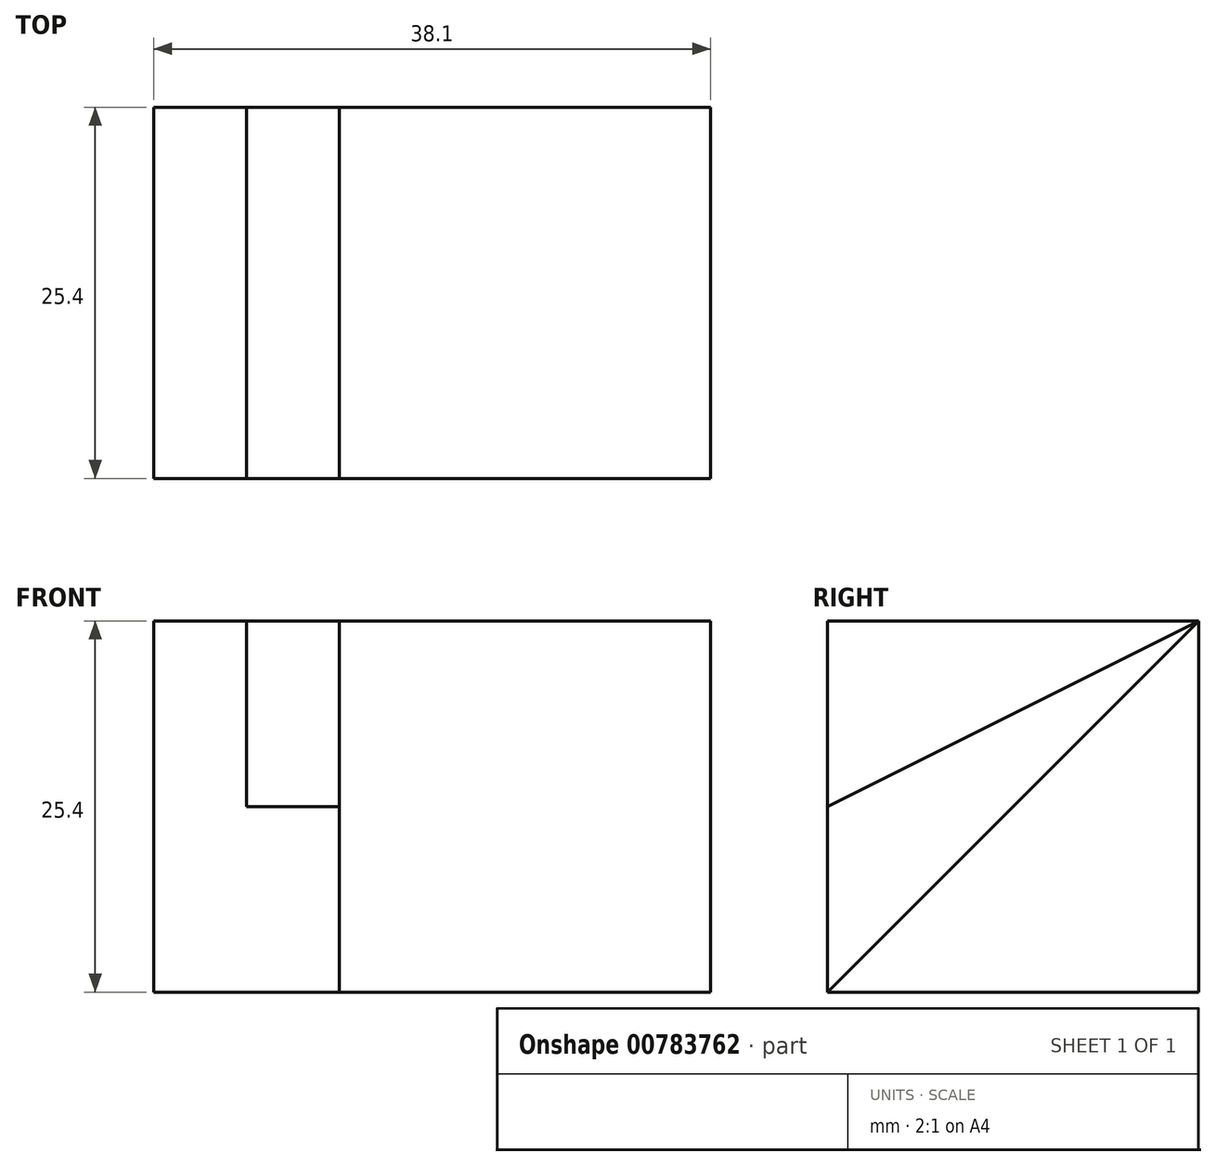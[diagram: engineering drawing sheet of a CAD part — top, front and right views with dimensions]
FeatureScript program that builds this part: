
annotation { "Feature Type Name" : "Feature", "Feature Type Description" : "" }
export const myFeature = defineFeature(function(context is Context, id is Id, definition is map)
    precondition{}
    {
        {
            var Q0;
            Q0=qCreatedBy(makeId("Front.planeOp"),FACE);
            var sketch = newSketch(context, id + "F0", { "sketchPlane" : qUnion([Q0])});
            skLineSegment(sketch, "E0", {"start": v(0, 0) * mm, "end": v(38.1, 0) * mm});
            skLineSegment(sketch, "E1", {"start": v(38.1, 0) * mm, "end": v(38.1, 25.4) * mm});
            skLineSegment(sketch, "E2", {"start": v(38.1, 25.4) * mm, "end": v(0, 25.4) * mm});
            skLineSegment(sketch, "E3", {"start": v(0, 25.4) * mm, "end": v(0, 0) * mm});
            skSolve(sketch);
        }
        {
            var Q0;
            Q0=makeQuery(id+"F0.imprint","IMPRINT",FACE,{"disambiguationData":[TD([[makeQuery(id+"F0.imprint","IMPRINT",EDGE,{"derivedFrom":sQuery(id+"F0.wireOp",EDGE,"E0")}),1.0]])]});
            extrude(context, id + "F1", {"entities" : qUnion([Q0]), "depth" : 25.4 * mm, "offsetDistance" : 25.4 * mm});
        }
        {
            var Q0;
            Q0=makeQuery(id+"F1.opExtrude","SWEPT_FACE",FACE,{"disambiguationData":[OSD([sQuery(id+"F0.wireOp",EDGE,"E1")])]});
            var sketch = newSketch(context, id + "F2", { "sketchPlane" : qUnion([Q0])});
            skLineSegment(sketch, "E4", {"start": v(0, 25.4) * mm, "end": v(-25.4, 0) * mm});
            skSolve(sketch);
        }
        {
            var Q0;
            Q0 = qSketchRegion(id + "F2", true);
            var Q1;
            Q1=makeQuery(id+"F2.imprint","IMPRINT",FACE,{"disambiguationData":[TD([[makeQuery(id+"F2.imprint","IMPRINT",EDGE,{"derivedFrom":sQuery(id+"F2.wireOp",EDGE,"E4")}),-1.0]])]});
            extrude(context, id + "F3", {"entities" : qUnion([Q0, Q1]), "operationType" : NewBodyOperationType.REMOVE, "oppositeDirection" : true, "depth" : 25.4 * mm, "offsetDistance" : 25.4 * mm});
        }
        {
            var Q0;
            Q0=makeQuery(id+"F3.boolean.opBoolean","COPY",FACE,{"derivedFrom":makeQuery(id+"F3.opExtrude","CAP_FACE",FACE,{"disambiguationData":[OSD([sQuery(id+"F0.wireOp",EDGE,"E1"),sQuery(id+"F0.wireOp",EDGE,"E2"),sQuery(id+"F2.wireOp",EDGE,"E4")])],"isStart":false})});
            var sketch = newSketch(context, id + "F4", { "sketchPlane" : qUnion([Q0])});
            skLineSegment(sketch, "E5", {"start": v(0, 25.4) * mm, "end": v(-25.4, 12.7) * mm});
            skSolve(sketch);
        }
        {
            var Q0;
            Q0 = qSketchRegion(id + "F4", true);
            var Q1;
            {var subQ0=sQuery(id+"F4.wireOp",EDGE,"E5");Q1=makeQuery(id+"F4.imprint","IMPRINT",FACE,{"disambiguationData":[TD([[makeQuery(id+"F4.imprint","IMPRINT",EDGE,{"derivedFrom":subQ0}),-1.0]])]});}
            extrude(context, id + "F5", {"entities" : qUnion([Q0, Q1]), "operationType" : NewBodyOperationType.REMOVE, "oppositeDirection" : true, "depth" : 6.35 * mm, "offsetDistance" : 25.4 * mm});
        }
    });
